# Revit family: 3.023645
name_source: partatom
category: Modelli generici
revit_build: Autodesk Revit 2017 (Build: 20160225_1515(x64)
units: mm (PartAtom-declared; Revit-internal decimal feet)

## family parameters
Basato su piano di lavoro = No
Condiviso = No
Punto di calcolo locali = No
Può ospitare armatura = No
Quota connettore circolare = Usa diametro
Sempre verticale = Sì
Taglio con vuoti quando caricato = No
Tipo di parte = Normale

## types (1)
- 3023645
    Commenti sul tipo = Machine side connections: DN 50 RIT DN 80 MAND
System side connections: DN 100
separator diameter with attacks: 668,00 mm
Wheelbases INAIL machine side: 359,00 mm
Wheelbases collector system side: 327 mm
    ETIM Note = Residential heating
    Machine side connections = DN 50 RIT DN 80 MAND
    Manufacturer Product Link = https://www.immergas.com
    MasterFormat = 23 00 00- Heating, Ventilating, and Air Conditioning (HVAC)
    Masterformat 2014 Description = Heating, Ventilating, and Air Conditioning (HVAC)
    Modello = 3023645
    Name BIM&CO = Caldaia
    Omniclass Description = HVAC Specific Products and Equipment
    Overall Height = 1059 mm  [stored 3.47441 ft]
    Overall Width = 1406 mm  [stored 4.61286 ft]
    Product Code = '3.023645
    Produttore = Immergas
    System side connections = DN 100
    Uniformat = Heat Generating Systems
    Uniformat II Description = Heat Generating Systems
    Uniformat code = D3020
    Wheelbases INAIL machine side = 359
    Wheelbases collector system side = 327
    separator diameter with attacks = 668

note: [stored X ft] marks values corroborated as IEEE doubles in the binary element streams (Revit-internal decimal feet)
